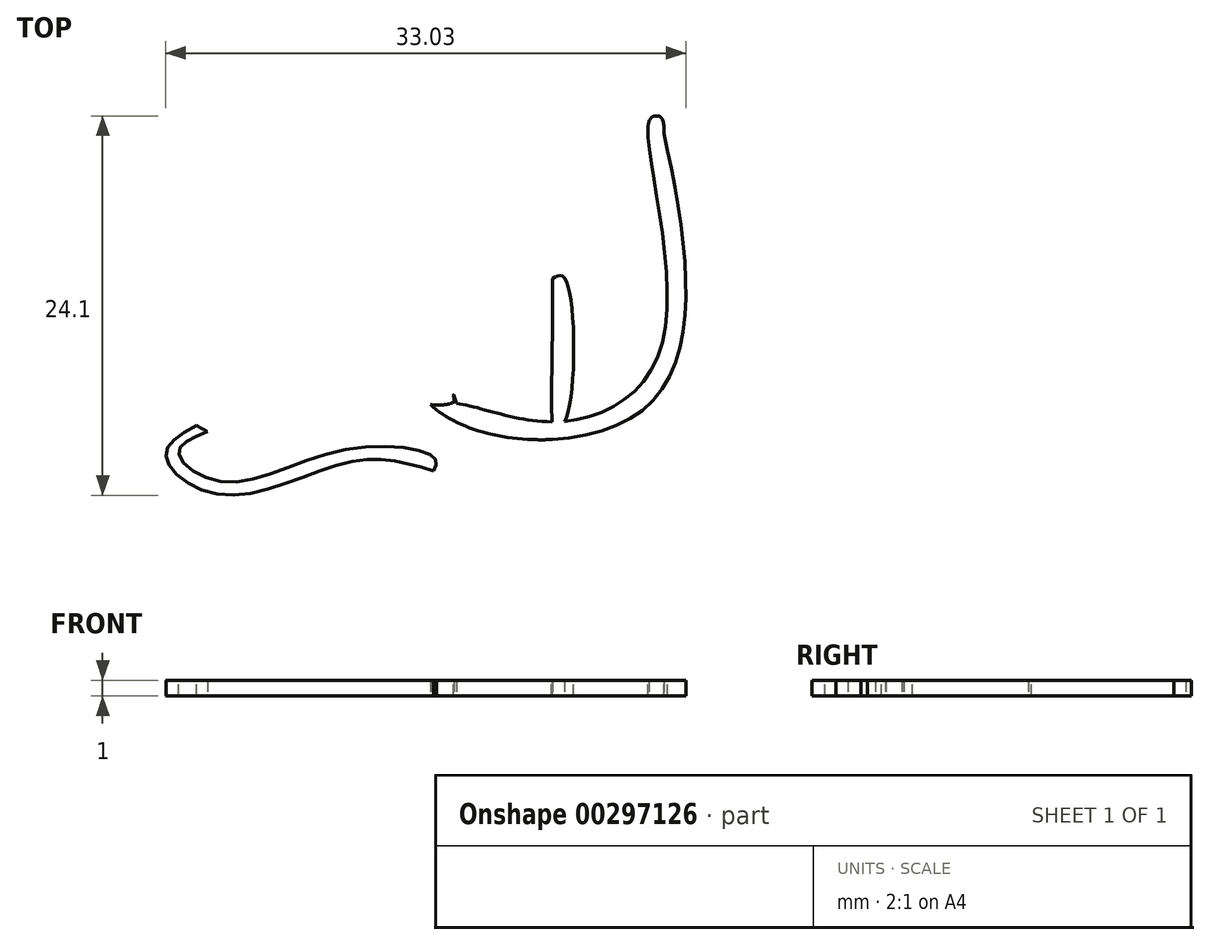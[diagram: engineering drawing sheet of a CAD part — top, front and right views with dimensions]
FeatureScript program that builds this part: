
annotation { "Feature Type Name" : "Feature", "Feature Type Description" : "" }
export const myFeature = defineFeature(function(context is Context, id is Id, definition is map)
    precondition{}
    {
        {
            var Q0;
            Q0=qCreatedBy(makeId("Top.planeOp"),FACE);
            var sketch = newSketch(context, id + "F0", { "sketchPlane" : qUnion([Q0])});
            skFitSpline(sketch, "E0", {"points": [v(28.59, 14.97) * mm, v(28.81, 17.4) * mm, v(26.98, 20.1) * mm, v(22.48, 19) * mm, v(21.58, 15.2) * mm, v(24.62, 12.98) * mm, v(25.5, 9.9) * mm, v(25.34, -1.95) * mm, v(25.46, -12.3) * mm, v(25.46, -12.3) * mm, v(12.2, -12.81) * mm, v(10.59, 4.92) * mm], "startDerivative": vector(12.62, 37.43) * mm, "endDerivative": vector(20.89, 106.85) * mm});
            skFitSpline(sketch, "E1", {"points": [v(12.2, -12.81) * mm, v(8.67, -15.43) * mm, v(12.2, -18.03) * mm, v(20.44, -15.93) * mm, v(25.66, -16.52) * mm], "startDerivative": vector(-21.85, -12.26) * mm, "endDerivative": vector(19.72, -5.96) * mm});
            skFitSpline(sketch, "E2", {"points": [v(18.67, -13.6) * mm, v(18.76, -4.15) * mm], "startDerivative": vector(0.08, 7.8) * mm, "endDerivative": vector(0.08, 7.8) * mm});
            skFitSpline(sketch, "E3", {"points": [v(33.22, -14.14) * mm, v(33.23, -4.31) * mm], "startDerivative": vector(-0.41, 7.37) * mm, "endDerivative": vector(-0.15, 7.36) * mm});
            skFitSpline(sketch, "E4", {"points": [v(28.59, 14.97) * mm, v(28.14, 14.97) * mm, v(28.07, 16.18) * mm, v(28, 16.8) * mm, v(25.47, 19.17) * mm, v(23.05, 18.22) * mm, v(22.37, 15.8) * mm, v(25.28, 13.8) * mm, v(27.2, 9.9) * mm, v(26.98, -1.67) * mm, v(26.93, -11.67) * mm, v(26.85, -12.2) * mm, v(25.46, -12.3) * mm], "startDerivative": vector(-15.9, -4.47) * mm, "endDerivative": vector(-9.4, 4.7) * mm});
            skFitSpline(sketch, "E5", {"points": [v(26.85, -12.2) * mm, v(33.19, -13.4) * mm, v(40.2, -8.34) * mm, v(39.36, 5.7) * mm, v(40.08, 5.92) * mm], "startDerivative": vector(17.8, -1.05) * mm, "endDerivative": vector(10.04, -2.29) * mm});
            skFitSpline(sketch, "E6", {"points": [v(33.23, -4.31) * mm, v(34.02, -4.31) * mm, v(33.98, -13.37) * mm, v(33.19, -13.4) * mm], "startDerivative": vector(4.62, 2.78) * mm, "endDerivative": vector(-4.16, 3.06) * mm});
            skFitSpline(sketch, "E7", {"points": [v(18.76, -4.15) * mm, v(19.5, -4.15) * mm, v(19.46, -13.51) * mm], "startDerivative": vector(3.74, 1.31) * mm, "endDerivative": vector(-1.39, -16.67) * mm});
            skFitSpline(sketch, "E8.trimOffspring", {"points": [v(28.59, 14.97) * mm, v(28.81, 17.4) * mm, v(26.98, 20.1) * mm, v(22.48, 19) * mm, v(21.58, 15.2) * mm, v(24.62, 12.98) * mm, v(25.5, 9.9) * mm, v(25.34, -1.95) * mm, v(25.46, -12.3) * mm, v(25.46, -12.3) * mm, v(12.2, -12.81) * mm, v(10.59, 4.92) * mm], "startDerivative": vector(12.62, 37.43) * mm, "endDerivative": vector(20.89, 106.85) * mm});
            skFitSpline(sketch, "E9.trimOffspring", {"points": [v(24.95, -12.31) * mm, v(18.18, -14.45) * mm, v(11.32, -14.03) * mm, v(8.04, -10.04) * mm, v(7.96, -0.75) * mm, v(9.46, 4.93) * mm], "startDerivative": vector(5.52, -15.73) * mm, "endDerivative": vector(8.28, 30.6) * mm});
            skFitSpline(sketch, "E10.trimOffspring", {"points": [v(25.34, -1.95) * mm, v(25.46, -12.3) * mm, v(39.36, -12.3) * mm, v(40.08, 5.92) * mm], "startDerivative": vector(-11.26, -39.92) * mm, "endDerivative": vector(-10.49, 47.6) * mm});
            skPoint(sketch, "E11.2.internal.orphan", {"position": v(18.76, -14.47) * mm});
            skFitSpline(sketch, "E12", {"points": [v(18.18, -14.45) * mm, v(33.22, -14.53) * mm], "startDerivative": vector(15.04, -0.07) * mm, "endDerivative": vector(15.04, -0.07) * mm});
            skFitSpline(sketch, "E13", {"points": [v(11.32, -14.03) * mm, v(9.49, -15.3) * mm, v(12.24, -17.2) * mm, v(20.16, -15.14) * mm, v(25.77, -15.75) * mm, v(25.66, -16.52) * mm], "startDerivative": vector(-17.2, -6.71) * mm, "endDerivative": vector(-4.41, -8.6) * mm});
            skFitSpline(sketch, "E14", {"points": [v(26.93, -11.67) * mm, v(27.13, -12.23) * mm], "startDerivative": vector(0.2, -0.57) * mm, "endDerivative": vector(0.2, -0.57) * mm});
            skFitSpline(sketch, "E15", {"points": [v(9.2, 4.02) * mm, v(9.44, 4.97) * mm, v(10.62, 4.98) * mm, v(10.38, 3.83) * mm, v(10.38, 3.83) * mm], "startDerivative": vector(-0.25, 3.43) * mm, "endDerivative": vector(0, -0.01) * mm});
            skPoint(sketch, "E16.0.internal.orphan", {"position": v(9.46, 4.92) * mm});
            skFitSpline(sketch, "E17", {"points": [v(39.28, 5.24) * mm, v(39.36, 5.7) * mm, v(39.62, 5.99) * mm, v(40.12, 5.92) * mm, v(40.3, 4.92) * mm], "startDerivative": vector(0.18, 2.1) * mm, "endDerivative": vector(-0.08, -3.74) * mm});
            skSolve(sketch);
        }
        {
            var Q0;
            Q0 = qSketchRegion(id + "F0", true);
            extrude(context, id + "F1", {"entities" : qUnion([Q0]), "depth" : 1 * mm});
        }
    });
